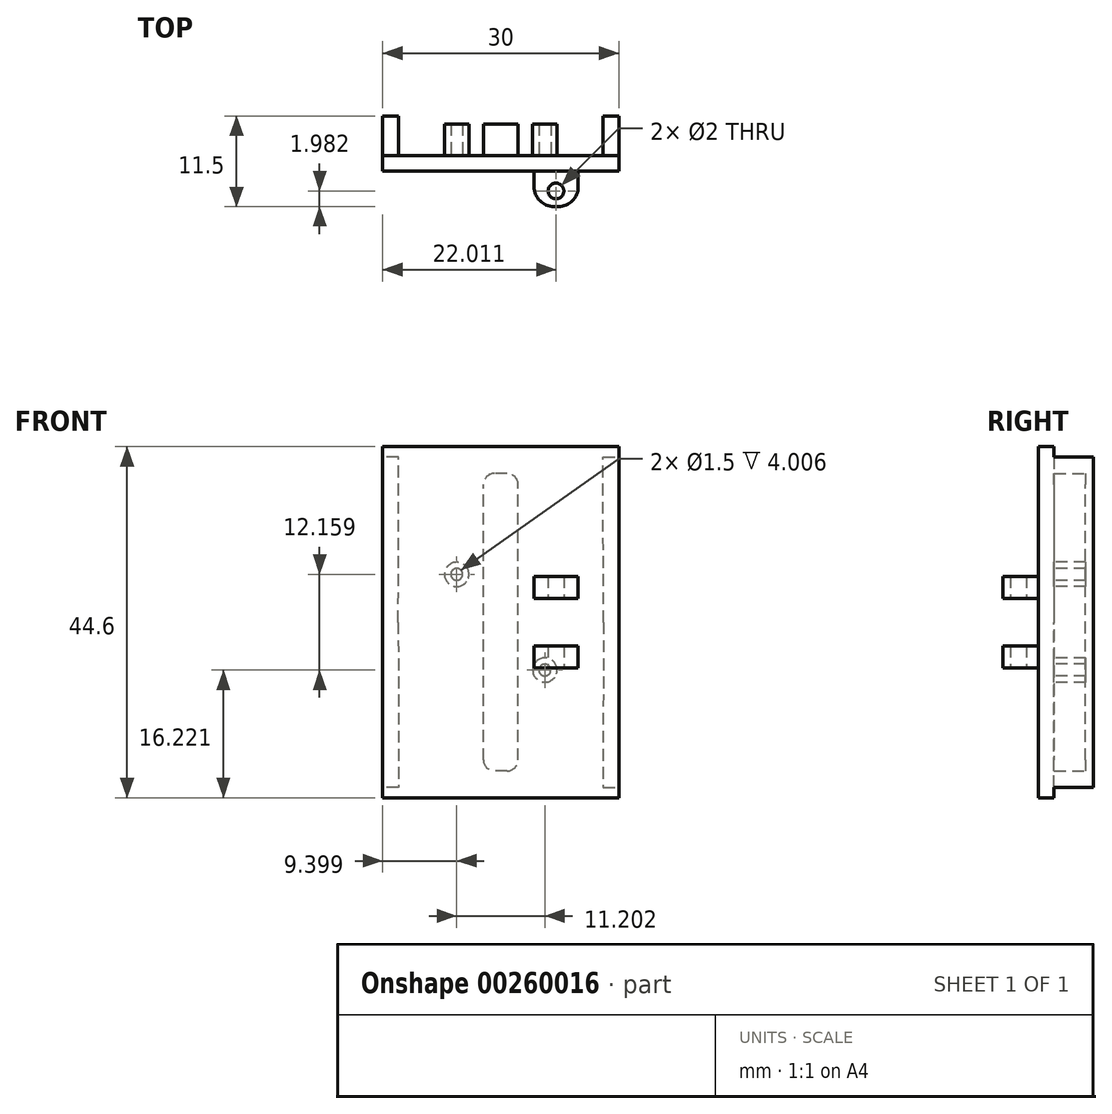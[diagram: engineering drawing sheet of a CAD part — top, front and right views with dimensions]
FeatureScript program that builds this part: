
annotation { "Feature Type Name" : "Feature", "Feature Type Description" : "" }
export const myFeature = defineFeature(function(context is Context, id is Id, definition is map)
    precondition{}
    {
        {
            var Q0;
            Q0=qCreatedBy(makeId("Front.planeOp"),FACE);
            var sketch = newSketch(context, id + "F0", { "sketchPlane" : qUnion([Q0])});
            skLineSegment(sketch, "E0.bottom", {"start": v(15, 22.3) * mm, "end": v(-15, 22.3) * mm});
            skLineSegment(sketch, "E0.top", {"start": v(15, -22.3) * mm, "end": v(-15, -22.3) * mm});
            skLineSegment(sketch, "E0.left", {"start": v(15, 22.3) * mm, "end": v(15, -22.3) * mm});
            skLineSegment(sketch, "E0.right", {"start": v(-15, 22.3) * mm, "end": v(-15, -22.3) * mm});
            skSolve(sketch);
        }
        {
            var Q0;
            Q0=makeQuery(id+"F0.imprint","IMPRINT",FACE,{"disambiguationData":[TD([[makeQuery(id+"F0.imprint","IMPRINT",EDGE,{"derivedFrom":sQuery(id+"F0.wireOp",EDGE,"E0.bottom")}),1.0]])]});
            extrude(context, id + "F1", {"entities" : qUnion([Q0]), "depth" : 8 * mm});
        }
        {
            var Q0;
            Q0=makeQuery(id+"F0.imprint","IMPRINT",FACE,{"disambiguationData":[TD([[makeQuery(id+"F0.imprint","IMPRINT",EDGE,{"derivedFrom":sQuery(id+"F0.wireOp",EDGE,"E0.bottom")}),1.0]])]});
            var sketch = newSketch(context, id + "F2", { "sketchPlane" : qUnion([Q0])});
            skLineSegment(sketch, "E1.0", {"start": v(15, 22.3) * mm, "end": v(0, 22.3) * mm});
            skLineSegment(sketch, "E2.0", {"start": v(15, 22.3) * mm, "end": v(15, 20.99) * mm});
            skLineSegment(sketch, "E3.top", {"start": v(15, 20.99) * mm, "end": v(13, 20.99) * mm});
            skPoint(sketch, "E4", {"position": v(15, 20.99) * mm});
            skLineSegment(sketch, "E5", {"start": v(13, 20.99) * mm, "end": v(13.02, 0) * mm});
            skLineSegment(sketch, "E6.bottom", {"start": v(-0.8, 18.9) * mm, "end": v(0.8, 18.9) * mm});
            skLineSegment(sketch, "E6.top", {"start": v(-0.8, -18.9) * mm, "end": v(0.8, -18.9) * mm});
            skLineSegment(sketch, "E6.left", {"start": v(-2.2, 17.5) * mm, "end": v(-2.2, -17.5) * mm});
            skLineSegment(sketch, "E6.right", {"start": v(2.2, 17.5) * mm, "end": v(2.2, -17.5) * mm});
            skPoint(sketch, "E6.middle", {"position": v(0, 0) * mm});
            skPoint(sketch, "E7.visualSharp", {"position": v(2.2, 18.9) * mm});
            skArc(sketch, "E7.filletArc", {"start": v(2.2, 17.5) * mm, "mid": v(1.8, 18.5) * mm, "end": v(0.8, 18.9) * mm});
            skPoint(sketch, "E8.visualSharp", {"position": v(-2.2, 18.9) * mm});
            skArc(sketch, "E8.filletArc", {"start": v(-0.8, 18.9) * mm, "mid": v(-1.8, 18.5) * mm, "end": v(-2.2, 17.5) * mm});
            skPoint(sketch, "E9.visualSharp", {"position": v(2.2, -18.9) * mm});
            skArc(sketch, "E9.filletArc", {"start": v(0.8, -18.9) * mm, "mid": v(1.8, -18.5) * mm, "end": v(2.2, -17.5) * mm});
            skPoint(sketch, "E10.visualSharp", {"position": v(-2.2, -18.9) * mm});
            skArc(sketch, "E10.filletArc", {"start": v(-2.2, -17.5) * mm, "mid": v(-1.8, -18.5) * mm, "end": v(-0.8, -18.9) * mm});
            skLineSegment(sketch, "E11.MirrorCS", {"start": v(-15, 22.3) * mm, "end": v(0, 22.3) * mm});
            skLineSegment(sketch, "E12.MirrorCS", {"start": v(-13, 20.99) * mm, "end": v(-13.02, 0) * mm});
            skLineSegment(sketch, "E13.MirrorCS", {"start": v(-15, 22.3) * mm, "end": v(-15, 20.99) * mm});
            skLineSegment(sketch, "E14.MirrorCS", {"start": v(-15, 20.99) * mm, "end": v(-13, 20.99) * mm});
            skLineSegment(sketch, "E15.MirrorCS", {"start": v(13, -20.99) * mm, "end": v(13.02, 0) * mm});
            skLineSegment(sketch, "E16.MirrorCS", {"start": v(15, -20.99) * mm, "end": v(13, -20.99) * mm});
            skLineSegment(sketch, "E17.MirrorCS", {"start": v(15, -22.3) * mm, "end": v(0, -22.3) * mm});
            skLineSegment(sketch, "E18.MirrorCS", {"start": v(-15, -22.3) * mm, "end": v(0, -22.3) * mm});
            skLineSegment(sketch, "E19.MirrorCS", {"start": v(-13, -20.99) * mm, "end": v(-13.02, 0) * mm});
            skLineSegment(sketch, "E20.MirrorCS", {"start": v(-15, -20.99) * mm, "end": v(-13, -20.99) * mm});
            skLineSegment(sketch, "E21.MirrorCS", {"start": v(-15, -22.3) * mm, "end": v(-15, -20.99) * mm});
            skLineSegment(sketch, "E22.MirrorCS", {"start": v(15, -22.3) * mm, "end": v(15, -20.99) * mm});
            skSolve(sketch);
        }
        {
            var Q0;
            Q0=makeQuery(id+"F2.imprint","IMPRINT",FACE,{"disambiguationData":[TD([[makeQuery(id+"F2.imprint","IMPRINT",EDGE,{"derivedFrom":sQuery(id+"F2.wireOp",EDGE,"E1.0")}),1.0]])]});
            extrude(context, id + "F3", {"entities" : qUnion([Q0]), "operationType" : NewBodyOperationType.REMOVE, "depth" : 6 * mm});
        }
        {
            var Q0;
            Q0=qCreatedBy(makeId("Top.planeOp"),FACE);
            var sketch = newSketch(context, id + "F4", { "sketchPlane" : qUnion([Q0])});
            skLineSegment(sketch, "E23.bottom", {"start": v(10.41, 0) * mm, "end": v(-10.59, 0) * mm});
            skLineSegment(sketch, "E23.top", {"start": v(10.41, -2) * mm, "end": v(-10.59, -2) * mm});
            skLineSegment(sketch, "E23.left", {"start": v(10.41, 0) * mm, "end": v(10.41, -2) * mm});
            skLineSegment(sketch, "E23.right", {"start": v(-10.59, 0) * mm, "end": v(-10.59, -2) * mm});
            skSolve(sketch);
        }
        {
            var Q0;
            Q0=makeQuery(id+"F1.opExtrude","CAP_FACE",FACE,{"disambiguationData":[OSD([sQuery(id+"F0.wireOp",EDGE,"E0.bottom"),sQuery(id+"F0.wireOp",EDGE,"E0.top"),sQuery(id+"F0.wireOp",EDGE,"E0.left"),sQuery(id+"F0.wireOp",EDGE,"E0.right")])],"isStart":false});
            var sketch = newSketch(context, id + "F5", { "sketchPlane" : qUnion([Q0])});
            skLineSegment(sketch, "E24.0.0", {"start": v(4.23, -5.78) * mm, "end": v(9.83, -5.78) * mm});
            skLineSegment(sketch, "E24.0.1", {"start": v(9.83, -5.78) * mm, "end": v(9.83, 5.82) * mm});
            skLineSegment(sketch, "E24.0.2", {"start": v(9.83, 5.82) * mm, "end": v(4.23, 5.82) * mm});
            skLineSegment(sketch, "E24.0.3", {"start": v(4.23, 5.82) * mm, "end": v(4.23, -5.78) * mm});
            skSolve(sketch);
        }
        {
            var Q0;
            Q0=makeQuery(id+"F5.imprint","IMPRINT",FACE,{"disambiguationData":[TD([[makeQuery(id+"F5.imprint","IMPRINT",EDGE,{"derivedFrom":sQuery(id+"F5.wireOp",EDGE,"E24.0.0")}),1.0]])]});
            extrude(context, id + "F6", {"entities" : qUnion([Q0]), "operationType" : NewBodyOperationType.ADD, "depth" : 4.5 * mm});
        }
        {
            var Q0;
            Q0=makeQuery(id+"F6.opExtrude","CAP_EDGE",EDGE,{"disambiguationData":[OSD([sQuery(id+"F5.wireOp",EDGE,"E24.0.3")])],"isStart":false});
            var Q1;
            Q1=makeQuery(id+"F6.opExtrude","CAP_EDGE",EDGE,{"disambiguationData":[OSD([sQuery(id+"F5.wireOp",EDGE,"E24.0.1")])],"isStart":false});
            fillet(context, id + "F7", {"entities" : qUnion([Q0, Q1]), "radius" : 2.53 * mm, "tangentPropagation" : true, "allowEdgeOverflow" : false});
        }
        {
            var Q0;
            Q0=qCreatedBy(makeId("Top.planeOp"),FACE);
            var sketch = newSketch(context, id + "F8", { "sketchPlane" : qUnion([Q0])});
            skCircle(sketch, "E25", {"center": v(7.01, -10.52) * mm, "radius": 1 * mm});
            skSolve(sketch);
        }
        {
            var Q0;
            Q0=qSketchRegion(id+"F8",true);
            extrude(context, id + "F9", {"entities" : qUnion([Q0]), "operationType" : NewBodyOperationType.REMOVE, "endBound" : BoundingType.SYMMETRIC, "depth" : 25 * mm});
        }
        {
            var Q0;
            Q0=qCreatedBy(makeId("Right.planeOp"),FACE);
            var sketch = newSketch(context, id + "F10", { "sketchPlane" : qUnion([Q0])});
            skLineSegment(sketch, "E26.bottom", {"start": v(-12.5, 3) * mm, "end": v(-8, 3) * mm});
            skLineSegment(sketch, "E26.top", {"start": v(-12.5, -3) * mm, "end": v(-8, -3) * mm});
            skLineSegment(sketch, "E26.left", {"start": v(-12.5, 3) * mm, "end": v(-12.5, -3) * mm});
            skLineSegment(sketch, "E26.right", {"start": v(-8, 3) * mm, "end": v(-8, -3) * mm});
            skPoint(sketch, "E26.middle", {"position": v(-10.26, 0) * mm});
            skSolve(sketch);
        }
        {
            var Q0;
            Q0=makeQuery(id+"F10.imprint","IMPRINT",FACE,{"disambiguationData":[TD([[makeQuery(id+"F10.imprint","IMPRINT",EDGE,{"derivedFrom":sQuery(id+"F10.wireOp",EDGE,"E26.bottom")}),-1.0]])]});
            extrude(context, id + "F11", {"entities" : qUnion([Q0]), "operationType" : NewBodyOperationType.REMOVE, "endBound" : BoundingType.SYMMETRIC, "oppositeDirection" : true, "depth" : 25 * mm});
        }
        {
            var Q0;
            Q0=qCreatedBy(makeId("Top.planeOp"),FACE);
            var sketch = newSketch(context, id + "F12", { "sketchPlane" : qUnion([Q0])});
            skLineSegment(sketch, "E27.bottom", {"start": v(-15.26, 0) * mm, "end": v(15.9, 0) * mm});
            skLineSegment(sketch, "E27.top", {"start": v(-15.26, -1) * mm, "end": v(15.9, -1) * mm});
            skLineSegment(sketch, "E27.left", {"start": v(-15.26, 0) * mm, "end": v(-15.26, -1) * mm});
            skLineSegment(sketch, "E27.right", {"start": v(15.9, 0) * mm, "end": v(15.9, -1) * mm});
            skSolve(sketch);
        }
        {
            var Q0;
            Q0=makeQuery(id+"F12.imprint","IMPRINT",FACE,{"disambiguationData":[TD([[makeQuery(id+"F12.imprint","IMPRINT",EDGE,{"derivedFrom":sQuery(id+"F12.wireOp",EDGE,"E27.bottom")}),-1.0]])]});
            extrude(context, id + "F13", {"entities" : qUnion([Q0]), "operationType" : NewBodyOperationType.REMOVE, "endBound" : BoundingType.SYMMETRIC, "depth" : 52.4 * mm});
        }
        {
            var Q0;
            Q0=qCreatedBy(makeId("Front.planeOp"),FACE);
            cPlane(context, id + "F14", {"entities" : qUnion([Q0]), "cplaneType" : CPlaneType.OFFSET, "offset" : 6 * mm, "width" : 150 * mm, "height" : 150 * mm});
        }
        {
            var Q0;
            Q0=qCreatedBy(id+"F14.planeOp",FACE);
            var sketch = newSketch(context, id + "F15", { "sketchPlane" : qUnion([Q0])});
            skCircle(sketch, "E28.MirrorC", {"center": v(5.6, -6.08) * mm, "radius": 0.75 * mm});
            skCircle(sketch, "E29.MirrorC", {"center": v(5.6, -6.08) * mm, "radius": 1.55 * mm});
            skCircle(sketch, "E30.MirrorC", {"center": v(-5.6, 6.08) * mm, "radius": 1.55 * mm});
            skCircle(sketch, "E31.MirrorC", {"center": v(-5.6, 6.08) * mm, "radius": 0.75 * mm});
            skSolve(sketch);
        }
        {
            var Q0;
            Q0=qSketchRegion(id+"F15",true);
            extrude(context, id + "F16", {"entities" : qUnion([Q0]), "operationType" : NewBodyOperationType.ADD, "oppositeDirection" : true, "depth" : 4.95 * mm});
        }
        {
            var Q0;
            Q0=makeQuery(id+"F4.imprint","IMPRINT",FACE,{"disambiguationData":[TD([[makeQuery(id+"F4.imprint","IMPRINT",EDGE,{"derivedFrom":sQuery(id+"F4.wireOp",EDGE,"E23.bottom")}),1.0]])]});
            extrude(context, id + "F17", {"entities" : qUnion([Q0]), "operationType" : NewBodyOperationType.REMOVE, "endBound" : BoundingType.SYMMETRIC, "oppositeDirection" : true, "depth" : 93 * mm});
        }
    });
